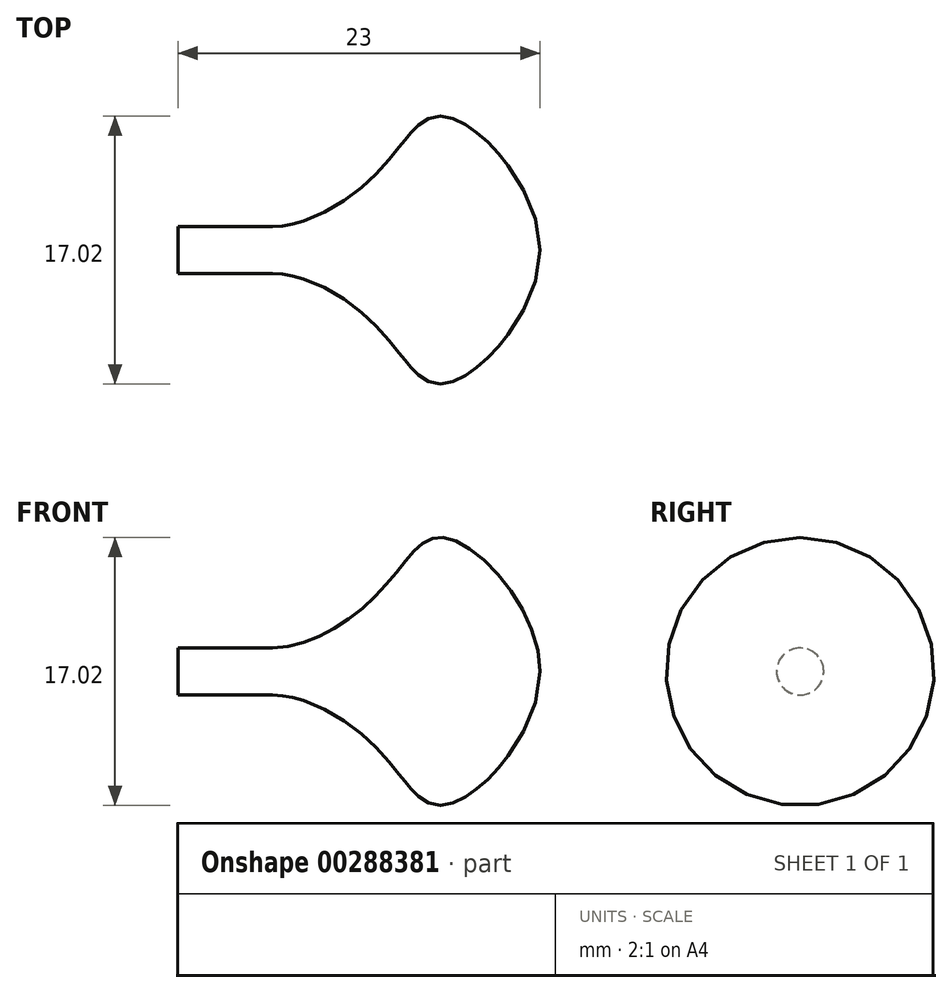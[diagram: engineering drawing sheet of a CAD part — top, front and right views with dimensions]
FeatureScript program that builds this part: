
annotation { "Feature Type Name" : "Feature", "Feature Type Description" : "" }
export const myFeature = defineFeature(function(context is Context, id is Id, definition is map)
    precondition{}
    {
        {
            var Q0;
            Q0=qCreatedBy(makeId("Front.planeOp"),FACE);
            var sketch = newSketch(context, id + "F0", { "sketchPlane" : qUnion([Q0])});
            skLineSegment(sketch, "E0", {"start": v(-8.68, 0) * mm, "end": v(25.97, 0) * mm, "construction": true});
            skLineSegment(sketch, "E1", {"start": v(0, 0) * mm, "end": v(0, 1.5) * mm});
            skLineSegment(sketch, "E2", {"start": v(0, 1.5) * mm, "end": v(6, 1.5) * mm});
            skFitSpline(sketch, "E3", {"points": [v(6, 1.5) * mm, v(13.2, 5.5) * mm, v(16.84, 8.5) * mm, v(23, 0) * mm], "startDerivative": vector(22.3, 0) * mm, "endDerivative": vector(0.44, -30.8) * mm});
            skLineSegment(sketch, "E4", {"start": v(23, 0) * mm, "end": v(23, 0) * mm});
            skLineSegment(sketch, "E5", {"start": v(0, 0) * mm, "end": v(23, 0) * mm});
            skSolve(sketch);
        }
        {
            var Q0;
            Q0=makeQuery(id+"F0.imprint","IMPRINT",FACE,{"disambiguationData":[TD([[makeQuery(id+"F0.imprint","IMPRINT",EDGE,{"derivedFrom":sQuery(id+"F0.wireOp",EDGE,"E1")}),-1.0]])]});
            var Q1;
            Q1=sQuery(id+"F0.wireOp",EDGE,"E1");
            var Q2;
            Q2=sQuery(id+"F0.wireOp",EDGE,"E2");
            var Q3;
            Q3=sQuery(id+"F0.wireOp",EDGE,"E3");
            var Q4;
            Q4=sQuery(id+"F0.wireOp",EDGE,"E0");
            revolve(context, id + "F1", {"entities" : qUnion([Q0]), "surfaceEntities" : qUnion([Q1, Q2, Q3]), "axis" : qUnion([Q4]), "revolveType" : RevolveType.FULL});
        }
    });
